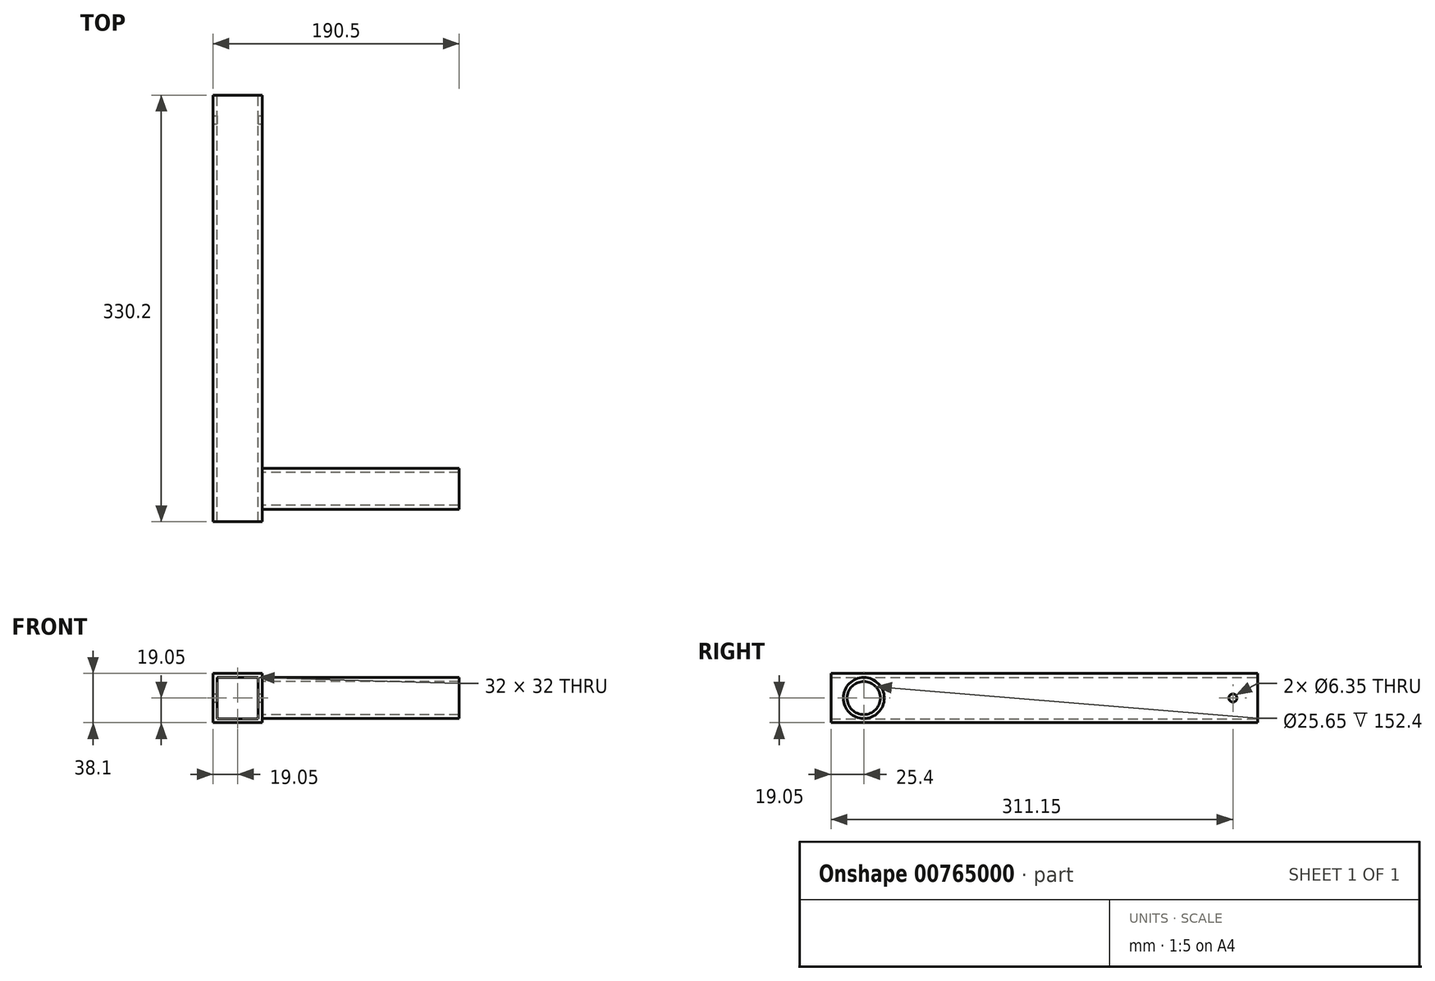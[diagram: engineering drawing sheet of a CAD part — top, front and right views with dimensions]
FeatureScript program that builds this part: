
annotation { "Feature Type Name" : "Feature", "Feature Type Description" : "" }
export const myFeature = defineFeature(function(context is Context, id is Id, definition is map)
    precondition{}
    {
        {
            var Q0;
            Q0=qCreatedBy(makeId("Front.planeOp"),FACE);
            var sketch = newSketch(context, id + "F0", { "sketchPlane" : qUnion([Q0])});
            skLineSegment(sketch, "E0.bottom", {"start": v(19.05, 19.05) * mm, "end": v(-19.05, 19.05) * mm});
            skLineSegment(sketch, "E0.top", {"start": v(19.05, -19.05) * mm, "end": v(-19.05, -19.05) * mm});
            skLineSegment(sketch, "E0.left", {"start": v(19.05, 19.05) * mm, "end": v(19.05, -19.05) * mm});
            skLineSegment(sketch, "E0.right", {"start": v(-19.05, 19.05) * mm, "end": v(-19.05, -19.05) * mm});
            skPoint(sketch, "E0.middle", {"position": v(0, 0) * mm});
            skLineSegment(sketch, "E1.0", {"start": v(16, -16) * mm, "end": v(-16, -16) * mm});
            skLineSegment(sketch, "E1.1", {"start": v(16, 16) * mm, "end": v(16, -16) * mm});
            skLineSegment(sketch, "E1.2", {"start": v(16, 16) * mm, "end": v(-16, 16) * mm});
            skLineSegment(sketch, "E1.3", {"start": v(-16, 16) * mm, "end": v(-16, -16) * mm});
            skSolve(sketch);
        }
        {
            var Q0;
            Q0 = qSketchRegion(id + "F0", true);
            extrude(context, id + "F1", {"entities" : qUnion([Q0]), "depth" : 330.2 * mm, "offsetDistance" : 25.4 * mm});
        }
        {
            var Q0;
            Q0=makeQuery(id+"F1.opExtrude","SWEPT_FACE",FACE,{"disambiguationData":[OSD([sQuery(id+"F0.wireOp",EDGE,"E0.left")])]});
            var sketch = newSketch(context, id + "F2", { "sketchPlane" : qUnion([Q0])});
            skCircle(sketch, "E2", {"center": v(-304.8, 0) * mm, "radius": 15.88 * mm});
            skCircle(sketch, "E3.0", {"center": v(-304.8, 0) * mm, "radius": 12.83 * mm});
            skSolve(sketch);
        }
        {
            var Q0;
            Q0 = qSketchRegion(id + "F2", true);
            extrude(context, id + "F3", {"entities" : qUnion([Q0]), "operationType" : NewBodyOperationType.ADD, "depth" : 152.4 * mm, "offsetDistance" : 25.4 * mm});
        }
        {
            var Q0;
            {var subQ0=sQuery(id+"F0.wireOp",EDGE,"E0.left");var subQ1=makeQuery(id+"F1.opExtrude","SWEPT_FACE",FACE,{"disambiguationData":[OSD([subQ0])]});var subQ2=sQuery(id+"F0.wireOp",EDGE,"E0.top");var subQ3=sQuery(id+"F0.wireOp",EDGE,"E0.bottom");Q0=makeQuery(id+"F3.boolean.opBoolean","SPLIT",FACE,{"disambiguationData":[TD([makeQuery(id+"F1.opExtrude","CAP_FACE",FACE,{"disambiguationData":[OSD([subQ3,subQ2,subQ0,sQuery(id+"F0.wireOp",EDGE,"E0.right"),sQuery(id+"F0.wireOp",EDGE,"E1.0"),sQuery(id+"F0.wireOp",EDGE,"E1.1"),sQuery(id+"F0.wireOp",EDGE,"E1.2"),sQuery(id+"F0.wireOp",EDGE,"E1.3")])],"isStart":true})])],"derivedFrom":subQ1});}
            var sketch = newSketch(context, id + "F4", { "sketchPlane" : qUnion([Q0])});
            skCircle(sketch, "E4", {"center": v(-19.05, 0) * mm, "radius": 3.18 * mm});
            skPoint(sketch, "E4.centerSnap0", {"position": v(0, 0) * mm});
            skSolve(sketch);
        }
        {
            var Q0;
            Q0 = qSketchRegion(id + "F4", true);
            extrude(context, id + "F5", {"entities" : qUnion([Q0]), "operationType" : NewBodyOperationType.REMOVE, "endBound" : BoundingType.THROUGH_ALL, "oppositeDirection" : true, "depth" : 25.4 * mm, "offsetDistance" : 25.4 * mm});
        }
    });
